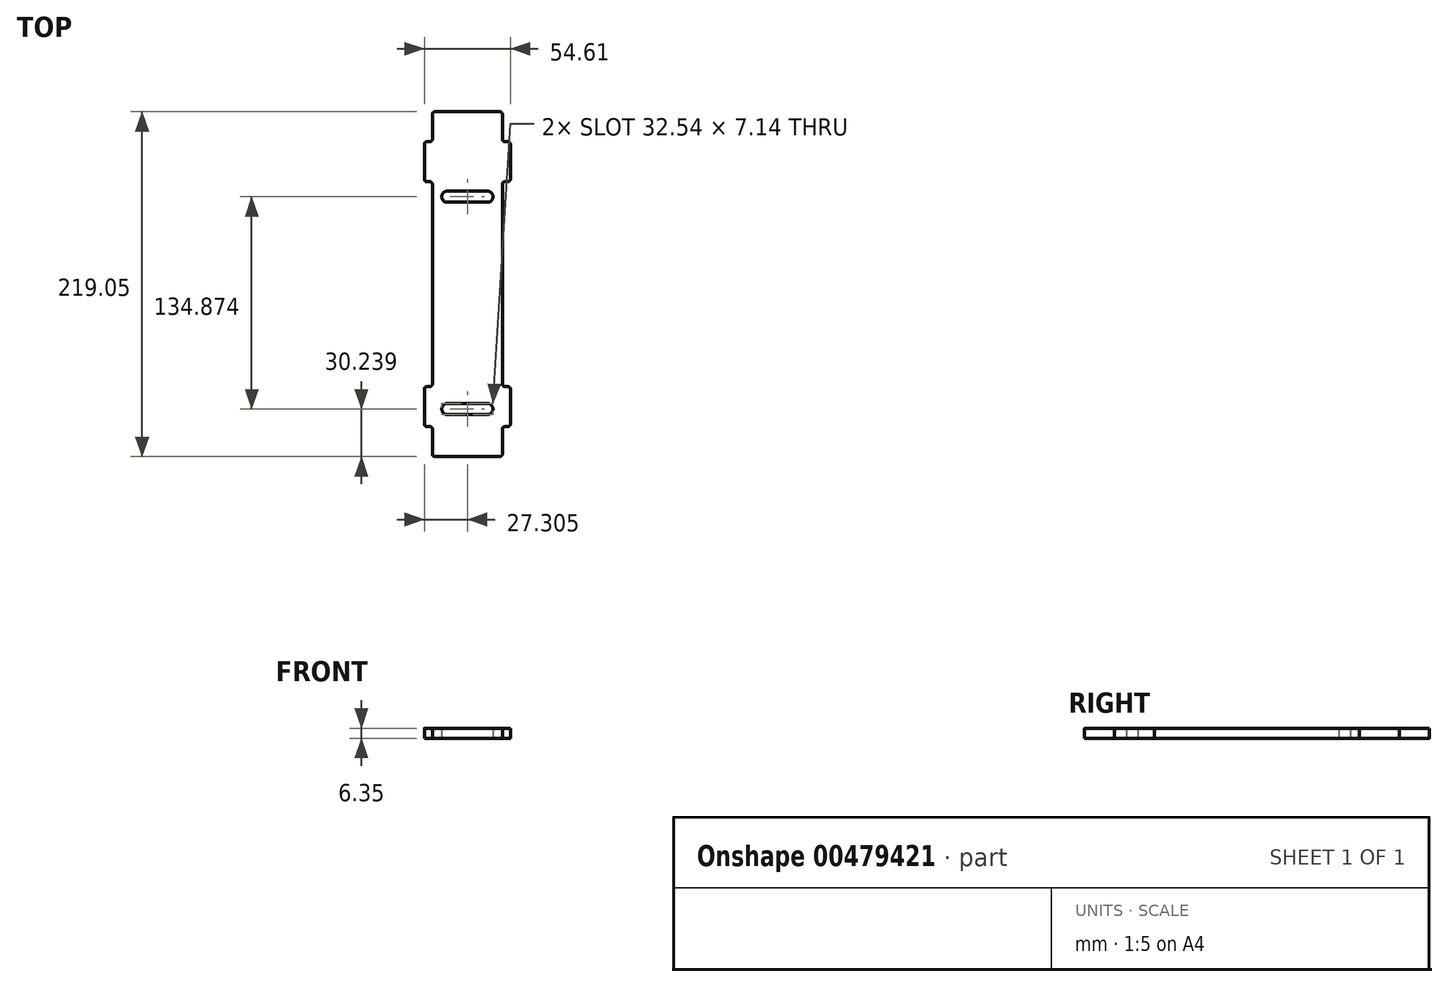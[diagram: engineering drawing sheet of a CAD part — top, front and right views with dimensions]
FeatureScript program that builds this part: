
annotation { "Feature Type Name" : "Feature", "Feature Type Description" : "" }
export const myFeature = defineFeature(function(context is Context, id is Id, definition is map)
    precondition{}
    {
        {
            var Q0;
            Q0=qCreatedBy(makeId("Top.planeOp"),FACE);
            var sketch = newSketch(context, id + "F0", { "sketchPlane" : qUnion([Q0])});
            skLineSegment(sketch, "E0", {"start": v(1.6, 0) * mm, "end": v(42.85, 0) * mm});
            skLineSegment(sketch, "E1", {"start": v(44.45, 1.6) * mm, "end": v(44.45, 17.45) * mm});
            skLineSegment(sketch, "E2", {"start": v(46.05, 19.05) * mm, "end": v(47.93, 19.05) * mm});
            skLineSegment(sketch, "E3", {"start": v(49.53, 20.65) * mm, "end": v(49.53, 42.85) * mm});
            skLineSegment(sketch, "E4", {"start": v(47.93, 44.45) * mm, "end": v(46.05, 44.45) * mm});
            skLineSegment(sketch, "E5", {"start": v(44.45, 46.05) * mm, "end": v(44.45, 173) * mm});
            skLineSegment(sketch, "E6", {"start": v(0, 173) * mm, "end": v(0, 46.05) * mm});
            skLineSegment(sketch, "E7", {"start": v(-1.6, 44.45) * mm, "end": v(-3.48, 44.45) * mm});
            skLineSegment(sketch, "E8", {"start": v(-5.08, 42.85) * mm, "end": v(-5.08, 20.65) * mm});
            skLineSegment(sketch, "E9", {"start": v(-3.48, 19.05) * mm, "end": v(-1.6, 19.05) * mm});
            skLineSegment(sketch, "E10", {"start": v(0, 17.45) * mm, "end": v(0, 1.6) * mm});
            skLineSegment(sketch, "E11", {"start": v(46.05, 174.6) * mm, "end": v(47.93, 174.6) * mm});
            skLineSegment(sketch, "E12", {"start": v(49.53, 176.2) * mm, "end": v(49.53, 198.4) * mm});
            skLineSegment(sketch, "E13", {"start": v(47.93, 200) * mm, "end": v(46.05, 200) * mm});
            skLineSegment(sketch, "E14", {"start": v(44.45, 201.6) * mm, "end": v(44.45, 217.45) * mm});
            skLineSegment(sketch, "E15", {"start": v(42.85, 219.05) * mm, "end": v(1.6, 219.05) * mm});
            skLineSegment(sketch, "E16", {"start": v(0, 217.45) * mm, "end": v(0, 201.6) * mm});
            skLineSegment(sketch, "E17", {"start": v(-1.6, 200) * mm, "end": v(-3.48, 200) * mm});
            skLineSegment(sketch, "E18", {"start": v(-5.08, 198.4) * mm, "end": v(-5.08, 176.2) * mm});
            skLineSegment(sketch, "E19", {"start": v(-3.48, 174.6) * mm, "end": v(-1.6, 174.6) * mm});
            skPoint(sketch, "E20.visualSharp", {"position": v(0, 219.05) * mm});
            skArc(sketch, "E20.filletArc", {"start": v(1.6, 219.05) * mm, "mid": v(0.47, 218.58) * mm, "end": v(0, 217.45) * mm});
            skPoint(sketch, "E21.visualSharp", {"position": v(44.45, 219.05) * mm});
            skArc(sketch, "E21.filletArc", {"start": v(44.45, 217.45) * mm, "mid": v(43.98, 218.58) * mm, "end": v(42.85, 219.05) * mm});
            skPoint(sketch, "E22.visualSharp", {"position": v(44.45, 200) * mm});
            skArc(sketch, "E22.filletArc", {"start": v(44.45, 201.6) * mm, "mid": v(44.92, 200.47) * mm, "end": v(46.05, 200) * mm});
            skPoint(sketch, "E23.visualSharp", {"position": v(49.53, 200) * mm});
            skArc(sketch, "E23.filletArc", {"start": v(49.53, 198.4) * mm, "mid": v(49.06, 199.53) * mm, "end": v(47.93, 200) * mm});
            skPoint(sketch, "E24.visualSharp", {"position": v(49.53, 174.6) * mm});
            skArc(sketch, "E24.filletArc", {"start": v(47.93, 174.6) * mm, "mid": v(49.06, 175.07) * mm, "end": v(49.53, 176.2) * mm});
            skPoint(sketch, "E25.visualSharp", {"position": v(44.45, 174.6) * mm});
            skArc(sketch, "E25.filletArc", {"start": v(46.05, 174.6) * mm, "mid": v(44.92, 174.13) * mm, "end": v(44.45, 173) * mm});
            skPoint(sketch, "E26.visualSharp", {"position": v(0, 174.6) * mm});
            skArc(sketch, "E26.filletArc", {"start": v(0, 173) * mm, "mid": v(-0.47, 174.13) * mm, "end": v(-1.6, 174.6) * mm});
            skPoint(sketch, "E27.visualSharp", {"position": v(-5.08, 174.6) * mm});
            skArc(sketch, "E27.filletArc", {"start": v(-5.08, 176.2) * mm, "mid": v(-4.61, 175.07) * mm, "end": v(-3.48, 174.6) * mm});
            skPoint(sketch, "E28.visualSharp", {"position": v(-5.08, 200) * mm});
            skArc(sketch, "E28.filletArc", {"start": v(-3.48, 200) * mm, "mid": v(-4.61, 199.53) * mm, "end": v(-5.08, 198.4) * mm});
            skPoint(sketch, "E29.visualSharp", {"position": v(0, 200) * mm});
            skArc(sketch, "E29.filletArc", {"start": v(-1.6, 200) * mm, "mid": v(-0.47, 200.47) * mm, "end": v(0, 201.6) * mm});
            skPoint(sketch, "E30.visualSharp", {"position": v(0, 44.45) * mm});
            skArc(sketch, "E30.filletArc", {"start": v(-1.6, 44.45) * mm, "mid": v(-0.47, 44.92) * mm, "end": v(0, 46.05) * mm});
            skPoint(sketch, "E31.visualSharp", {"position": v(-5.08, 44.45) * mm});
            skArc(sketch, "E31.filletArc", {"start": v(-3.48, 44.45) * mm, "mid": v(-4.61, 43.98) * mm, "end": v(-5.08, 42.85) * mm});
            skPoint(sketch, "E32.visualSharp", {"position": v(-5.08, 19.05) * mm});
            skArc(sketch, "E32.filletArc", {"start": v(-5.08, 20.65) * mm, "mid": v(-4.61, 19.52) * mm, "end": v(-3.48, 19.05) * mm});
            skPoint(sketch, "E33.visualSharp", {"position": v(0, 19.05) * mm});
            skArc(sketch, "E33.filletArc", {"start": v(0, 17.45) * mm, "mid": v(-0.47, 18.58) * mm, "end": v(-1.6, 19.05) * mm});
            skPoint(sketch, "E34.visualSharp", {"position": v(0, 0) * mm});
            skArc(sketch, "E34.filletArc", {"start": v(0, 1.6) * mm, "mid": v(0.47, 0.47) * mm, "end": v(1.6, 0) * mm});
            skPoint(sketch, "E35.visualSharp", {"position": v(44.45, 0) * mm});
            skArc(sketch, "E35.filletArc", {"start": v(42.85, 0) * mm, "mid": v(43.98, 0.47) * mm, "end": v(44.45, 1.6) * mm});
            skPoint(sketch, "E36.visualSharp", {"position": v(44.45, 19.05) * mm});
            skArc(sketch, "E36.filletArc", {"start": v(46.05, 19.05) * mm, "mid": v(44.92, 18.58) * mm, "end": v(44.45, 17.45) * mm});
            skPoint(sketch, "E37.visualSharp", {"position": v(49.53, 19.05) * mm});
            skArc(sketch, "E37.filletArc", {"start": v(47.93, 19.05) * mm, "mid": v(49.06, 19.52) * mm, "end": v(49.53, 20.65) * mm});
            skPoint(sketch, "E38.visualSharp", {"position": v(49.53, 44.45) * mm});
            skArc(sketch, "E38.filletArc", {"start": v(49.53, 42.85) * mm, "mid": v(49.06, 43.98) * mm, "end": v(47.93, 44.45) * mm});
            skPoint(sketch, "E39.visualSharp", {"position": v(44.45, 44.45) * mm});
            skArc(sketch, "E39.filletArc", {"start": v(44.45, 46.05) * mm, "mid": v(44.92, 44.92) * mm, "end": v(46.05, 44.45) * mm});
            skCircle(sketch, "E40", {"center": v(9.52, 30.24) * mm, "radius": 3.57 * mm});
            skCircle(sketch, "E41", {"center": v(34.93, 30.24) * mm, "radius": 3.57 * mm});
            skLineSegment(sketch, "E42", {"start": v(9.52, 33.8) * mm, "end": v(34.93, 33.8) * mm});
            skLineSegment(sketch, "E43", {"start": v(9.52, 26.67) * mm, "end": v(34.93, 26.67) * mm});
            skCircle(sketch, "E44", {"center": v(9.53, 165.11) * mm, "radius": 3.57 * mm});
            skCircle(sketch, "E45", {"center": v(34.92, 165.11) * mm, "radius": 3.57 * mm});
            skLineSegment(sketch, "E46", {"start": v(9.53, 161.54) * mm, "end": v(34.92, 161.54) * mm});
            skLineSegment(sketch, "E47", {"start": v(9.53, 168.68) * mm, "end": v(34.92, 168.68) * mm});
            skSolve(sketch);
        }
        {
            var Q0;
            Q0=qSketchRegion(id+"F0",true);
            extrude(context, id + "F1", {"entities" : qUnion([Q0]), "depth" : 6.35 * mm, "offsetDistance" : 25.4 * mm});
        }
    });
